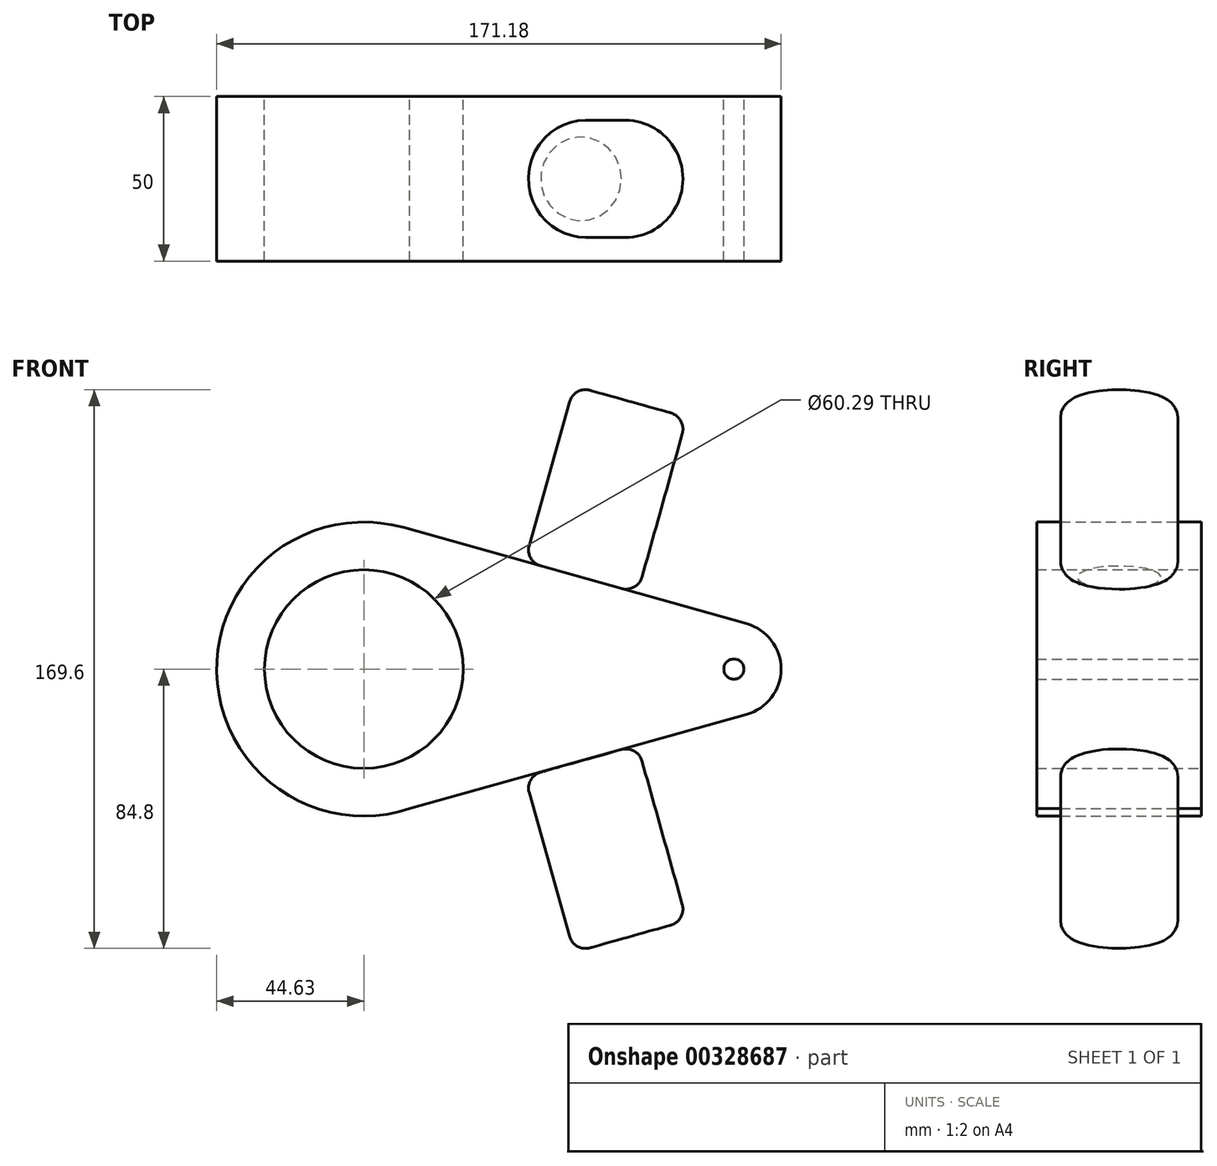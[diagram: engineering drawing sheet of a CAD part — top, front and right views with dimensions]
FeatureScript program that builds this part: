
annotation { "Feature Type Name" : "Feature", "Feature Type Description" : "" }
export const myFeature = defineFeature(function(context is Context, id is Id, definition is map)
    precondition{}
    {
        {
            var Q0;
            Q0=qCreatedBy(makeId("Front.planeOp"),FACE);
            var sketch = newSketch(context, id + "F0", { "sketchPlane" : qUnion([Q0])});
            skCircle(sketch, "E0", {"center": v(0, 0) * mm, "radius": 44.63 * mm});
            skCircle(sketch, "E1", {"center": v(112.24, 0) * mm, "radius": 3.06 * mm});
            skCircle(sketch, "E2", {"center": v(112.24, 0) * mm, "radius": 14.3 * mm});
            skLineSegment(sketch, "E3", {"start": v(12.06, 42.97) * mm, "end": v(116.1, 13.77) * mm});
            skLineSegment(sketch, "E4", {"start": v(13.94, -42.4) * mm, "end": v(116.1, -13.77) * mm});
            skCircle(sketch, "E5", {"center": v(0, 0) * mm, "radius": 30.14 * mm});
            skSolve(sketch);
        }
        {
            var Q0;
            Q0 = qSketchRegion(id + "F0", true);
            extrude(context, id + "F1", {"entities" : qUnion([Q0]), "depth" : 50 * mm});
        }
        {
            var Q0;
            Q0=makeQuery(id+"F1.opExtrude","SWEPT_FACE",FACE,{"disambiguationData":[OSD([sQuery(id+"F0.wireOp",EDGE,"E3")])]});
            var sketch = newSketch(context, id + "F2", { "sketchPlane" : qUnion([Q0])});
            skCircle(sketch, "E6", {"center": v(55.91, -25) * mm, "radius": 17.78 * mm});
            skPoint(sketch, "E6.centerSnap0", {"position": v(108.07, -25) * mm});
            skSolve(sketch);
        }
        {
            var Q0;
            Q0 = qSketchRegion(id + "F2", true);
            extrude(context, id + "F3", {"entities" : qUnion([Q0]), "depth" : 55.37 * mm});
        }
        {
            var Q0;
            Q0=makeQuery(id+"F3.opExtrude","CAP_FACE",FACE,{"disambiguationData":[OSD([sQuery(id+"F2.wireOp",EDGE,"E6")])],"isStart":false});
            var Q1;
            Q1=makeQuery(id+"F3.opExtrude","CAP_EDGE",EDGE,{"disambiguationData":[OSD([sQuery(id+"F2.wireOp",EDGE,"E6")])],"isStart":true});
            fillet(context, id + "F4", {"entities" : qUnion([Q0, Q1]), "radius" : 5.08 * mm, "tangentPropagation" : true, "allowEdgeOverflow" : false});
        }
        {
            var Q0;
            Q0=makeQuery(id+"F3.opExtrude","SWEPT_BODY",BODY,{"disambiguationData":[OSD([sQuery(id+"F2.wireOp",EDGE,"E6")])]});
            var Q1;
            Q1=qCreatedBy(makeId("Top.planeOp"),FACE);
            mirror(context, id + "F5", {"operationType" : NewBodyOperationType.ADD, "entities" : qUnion([Q0]), "mirrorPlane" : qUnion([Q1])});
        }
    });
